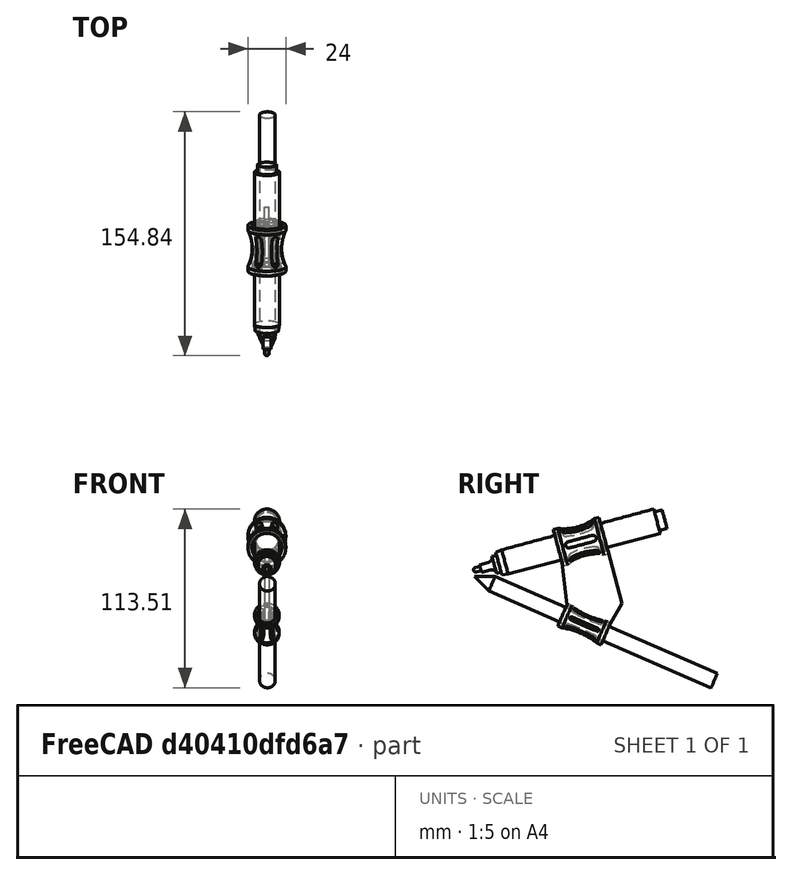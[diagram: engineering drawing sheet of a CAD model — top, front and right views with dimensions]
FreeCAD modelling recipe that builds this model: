
FCSTD DOCUMENT  (FreeCAD 1.0R39109 (Git))
Label: marker_holder_01
License: All rights reserved
LicenseURL: http://www.ohwr.org/attachments/2388/cern_ohl_v_1_2.txt
objects: PartDesign::SubShapeBinder×8, Sketcher::SketchObject×7, PartDesign::Plane×7, PartDesign::Body×5, PartDesign::Revolution×4, PartDesign::Line×3, PartDesign::Pocket×2, PartDesign::PolarPattern×2, PartDesign::Point×2, Mesh::Feature×1, PartDesign::Pad×1
note: 64 computed .brp shape members not serialized (recipe doc carries the construction recipe); baked Part::Feature solids carry a one-line shape summary decoded from their .brp

FEATURE [Mesh::Feature] Pencil_Hand_Pack
  Placement = pos=(0,0,0) rot=(-0.762035,0.457877,-0.457877;1.83927rad)
FEATURE [Sketcher::SketchObject] Sketch
  ArcFitTolerance = 1e-06
  AttachmentSupport = -> [YZ_Plane001]
  FullyConstrained = true
  MakeInternals = false
  MapMode = 5
  Placement = pos=(0,0,0) rot=(0.57735,0.57735,0.57735;2.0944rad)
  sketch-geometry (14):
    g0: LineSegment StartX=125.5 StartY=2e-16 StartZ=0 EndX=125.5 EndY=6 EndZ=0
    g1: LineSegment StartX=125.5 StartY=6 StartZ=0 EndX=120.5 EndY=6 EndZ=0
    g2: LineSegment StartX=120.5 StartY=6 StartZ=0 EndX=120.5 EndY=8 EndZ=0
    g3: LineSegment StartX=120.5 StartY=8 StartZ=0 EndX=28.5 EndY=8 EndZ=0
    g4: LineSegment StartX=28.5 StartY=8 StartZ=0 EndX=20.5 EndY=8 EndZ=0
    g5: LineSegment StartX=20.5 StartY=8 StartZ=0 EndX=16.5 EndY=7.5 EndZ=0
    g6: LineSegment StartX=16.5 StartY=7.5 StartZ=0 EndX=16.5 EndY=5.5 EndZ=0
    g7: LineSegment StartX=16.5 StartY=5.5 StartZ=0 EndX=13.5 EndY=5.5 EndZ=0
    g8: ArcOfCircle CenterX=10.5 CenterY=5.5 CenterZ=0 NormalX=0 NormalY=0 NormalZ=1 AngleXU=0 Radius=3 StartAngle=4.71239 EndAngle=6.28319
    g9: LineSegment StartX=10.5 StartY=2.5 StartZ=0 EndX=4.5 EndY=2.5 EndZ=0
    g10: LineSegment StartX=4.5 StartY=2.5 StartZ=0 EndX=4.5 EndY=1.5 EndZ=0
    g11: LineSegment StartX=4.5 StartY=1.5 StartZ=0 EndX=1.5 EndY=1.5 EndZ=0
    g12: ArcOfCircle CenterX=1.5 CenterY=0 CenterZ=0 NormalX=0 NormalY=0 NormalZ=1 AngleXU=0 Radius=1.5 StartAngle=1.5708 EndAngle=3.14159
    g13: LineSegment StartX=0 StartY=2e-16 StartZ=0 EndX=125.5 EndY=2e-16 EndZ=0
  constraints (40):
    c: Vertical(g0)
    c: Coincident(g0,g1)
    c: Horizontal(g1)
    c: Coincident(g1,g2)
    c: Vertical(g2)
    c: Coincident(g2,g3)
    c: Horizontal(g3)
    c: Coincident(g3,g4)
    c: Horizontal(g4)
    c: Coincident(g4,g5)
    c: Coincident(g5,g6)
    c: Vertical(g6)
    c: Coincident(g6,g7)
    c: Horizontal(g7)
    c: Perpendicular(g7,g8) = 4.71239
    c: Horizontal(g9)
    c: Coincident(g9,g10)
    c: Coincident(g10,g11)
    c: Horizontal(g11)
    c: Tangent(g11,g12) = -1.5708
    c: Perpendicular(g12,g-1)
    c: Radius(g12) = 1.5
    c: DistanceX(g11,g11) = 3
    c: Vertical(g10)
    c: Distance(g10,g10) = 1
    c: DistanceX(g9,g9) = 6
    c: Tangent(g8,g9) = 1.5708
    c: Radius(g8) = 3
    c: DistanceX(g7,g7) = 3
    c: DistanceX(g5,g4) = 4
    c: DistanceX(g4,g4) = 8
    c: DistanceX(g3,g3) = 92
    c: DistanceX(g1,g1) = 5
    c: DistanceY(g0,g0) = 6
    c: Distance(g2,g-1) = 8
    c: Coincident(g12,g-1)
    c: DistanceY(g5,g4) = 0.5
    c: Coincident(g13,g12)
    c: Coincident(g13,g0)
    c: Horizontal(g13)
FEATURE [PartDesign::Revolution] Revolution
  Angle = 360
  Angle2 = 60
  Axis = (0,1,0)
  Base = (0,0,0)
  Placement = pos=(0,0,0) rot=(1,1,1;2.0944rad)
  Profile = -> Sketch
  ReferenceAxis = -> Sketch [H_Axis]
  Refine = true
  Suppressed = false
  Type = 0
FEATURE [PartDesign::Body] Body001  label="Marker"
  AllowCompound = false
  Group = -> [Sketch,Revolution]
  Origin = -> Origin001
  Placement = pos=(74.7,-42.8,49.3) rot=(1,0,0;0.261799rad)
  Tip = -> Revolution
FEATURE [PartDesign::SubShapeBinder] Binder
  BindCopyOnChange = 0
  BindMode = 0
  ClaimChildren = false
  Context = -> Body [Binder.]
  Fuse = false
  MakeFace = true
  OffsetFill = false
  OffsetIntersection = false
  OffsetJoinType = 0
  OffsetOpenResult = false
  PartialLoad = false
  Refine = true
  Relative = true
  Support = -> [Body001]
  _Version = 2
FEATURE [PartDesign::Line] DatumLine
  AttacherType = Attacher::AttachEngineLine
  AttachmentSupport = -> [Binder]
  Length = 20
  MapMode = 19
  Placement = pos=(74.7,78.4237,81.7818) rot=(-0.519988,-0.519988,-0.677661;1.95044rad)
  ResizeMode = 0
FEATURE [PartDesign::Plane] DatumPlane
  AttachmentOffset = pos=(0,0,0) rot=(1,0,0;1.5708rad)
  AttachmentSupport = -> [DatumLine]
  Length = 131.506
  MapMode = 7
  Placement = pos=(74.7,78.4237,81.7818) rot=(1,0,0;3.40339rad)
  ResizeMode = 0
  Width = 193.795
FEATURE [PartDesign::Plane] DatumPlane001
  AttachmentSupport = -> [DatumLine]
  Length = 139.497
  MapMode = 3
  Placement = pos=(74.7,78.4237,81.7818) rot=(0.129428,-0.983106,-0.129428;1.58783rad)
  ResizeMode = 0
  Width = 194.678
FEATURE [PartDesign::Line] DatumLine001
  AttacherType = Attacher::AttachEngineLine
  AttachmentOffset = pos=(0,-104,0) rot=(1,0,0;0.671952rad)
  AttachmentSupport = -> [DatumLine]
  Length = 20
  MapMode = 29
  Placement = pos=(74.7,105.341,-18.6745) rot=(0,0.836286,0.548293;3.14159rad)
  ResizeMode = 0
FEATURE [Sketcher::SketchObject] Sketch001
  ArcFitTolerance = 1e-06
  AttachmentOffset = pos=(0,0,75) rot=(0,0,1;0rad)
  AttachmentSupport = -> [YZ_Plane]
  ExternalGeometry = -> [DatumLine,DatumLine001]
  FullyConstrained = true
  MakeInternals = false
  MapMode = 5
  Placement = pos=(75,0,0) rot=(0.57735,0.57735,0.57735;2.0944rad)
  sketch-geometry (4):
    g0: LineSegment StartX=108.006 StartY=-25.2856 StartZ=0 EndX=-33.221 EndY=36.1217 EndZ=0
    g1: LineSegment StartX=-33.221 StartY=36.1217 StartZ=0 EndX=-42.232 EndY=45.492 EndZ=0
    g2: LineSegment StartX=-42.232 StartY=45.492 StartZ=0 EndX=110 EndY=-20.7003 EndZ=0
    g3: LineSegment StartX=108.006 StartY=-25.2856 StartZ=0 EndX=110 EndY=-20.7003 EndZ=0
  constraints (12):
    c: Coincident(g0,g1)
    c: Coincident(g1,g2)
    c: PointOnObject(g1,g-4)
    c: Distance(g2,g0) = 5
    c: Coincident(g3,g0)
    c: Coincident(g3,g2)
    c: PointOnObject(g2,g-4)
    c: Perpendicular(g2,g3)
    c: Perpendicular(g0,g3)
    c: DistanceX(g2) = 110
    c: Distance(g2,g2) = 166
    c: Distance(g0,g0) = 154
FEATURE [PartDesign::Revolution] Revolution001
  Angle = 360
  Angle2 = 60
  Axis = (0,0.91706,-0.398749)
  Base = (75,-42.232,45.492)
  Placement = pos=(0,0,0) rot=(1,1,1;2.0944rad)
  Profile = -> Sketch001
  ReferenceAxis = -> Sketch001 [Edge3]
  Refine = true
  Reversed = true
  Suppressed = false
  Type = 0
FEATURE [PartDesign::Body] Body  label="Pencil"
  AllowCompound = false
  Group = -> [Binder,DatumLine,DatumPlane,DatumPlane001,DatumLine001,Sketch001,Revolution001]
  Origin = -> Origin
  Tip = -> Revolution001
FEATURE [PartDesign::SubShapeBinder] Binder001
  BindCopyOnChange = 0
  BindMode = 0
  ClaimChildren = false
  Context = -> Body002 [Binder001.]
  Fuse = false
  MakeFace = true
  OffsetFill = false
  OffsetIntersection = false
  OffsetJoinType = 0
  OffsetOpenResult = false
  PartialLoad = false
  Refine = true
  Relative = true
  Support = -> [Body]
  _Version = 2
FEATURE [PartDesign::SubShapeBinder] Binder002
  BindCopyOnChange = 0
  BindMode = 0
  ClaimChildren = false
  Context = -> Body002 [Binder002.]
  Fuse = false
  MakeFace = true
  OffsetFill = false
  OffsetIntersection = false
  OffsetJoinType = 0
  OffsetOpenResult = false
  PartialLoad = false
  Refine = true
  Relative = true
  Support = -> [Body001]
  _Version = 2
FEATURE [PartDesign::Plane] DatumPlane002
  AttachmentOffset = pos=(0,0,-78) rot=(0,0,1;0rad)
  AttachmentSupport = -> [Binder001]
  Length = 130.818
  MapMode = 5
  Placement = pos=(1.42e-14,28.5489,-12.4134) rot=(0,0.836286,0.548293;3.14159rad)
  ResizeMode = 0
  Width = 149.719
FEATURE [PartDesign::Plane] DatumPlane003
  AttachmentOffset = pos=(0,0,-40) rot=(0,0,1;0rad)
  AttachmentSupport = -> [Binder002]
  Length = 129.082
  MapMode = 5
  Placement = pos=(0,54.9787,14.7315) rot=(0,0.608761,0.793353;3.14159rad)
  ResizeMode = 0
  Width = 129.861
FEATURE [PartDesign::Plane] DatumPlane005
  AttachmentOffset = pos=(0,0,0) rot=(0,1,0;1.5708rad)
  AttachmentSupport = -> [Binder001]
  Length = 198.944
  MapMode = 7
  Placement = pos=(75,108.006,-25.2856) rot=(-0.480769,0.733295,0.480769;4.40704rad)
  ResizeMode = 0
  Width = 155.693
FEATURE [Sketcher::SketchObject] Sketch002
  ArcFitTolerance = 1e-06
  AttachmentSupport = -> [DatumPlane005]
  ExternalGeometry = -> [Binder001]
  FullyConstrained = true
  MakeInternals = false
  MapMode = 5
  Placement = pos=(75,108.006,-25.2856) rot=(0.480769,-0.733295,-0.480769;1.87614rad)
  sketch-geometry (11):
    g0: LineSegment [constr] StartX=166 StartY=5 StartZ=0 EndX=1.137e-13 EndY=5 EndZ=0
    g1: LineSegment StartX=105 StartY=-0.8 StartZ=0 EndX=105 EndY=-2.8 EndZ=0
    g2: LineSegment StartX=105 StartY=-2.8 StartZ=0 EndX=102 EndY=-2.8 EndZ=0
    g3: ArcOfCircle CenterX=90 CenterY=-93.95 CenterZ=0 NormalX=0 NormalY=0 NormalZ=1 AngleXU=0 Radius=94.35 StartAngle=1.41114 EndAngle=1.73046
    g4: LineSegment StartX=75 StartY=-0.8 StartZ=0 EndX=75 EndY=-2.8 EndZ=0
    g5: LineSegment [constr] StartX=75 StartY=-0.8 StartZ=0 EndX=105 EndY=-0.8 EndZ=0
    g6: LineSegment [constr] StartX=90 StartY=-93.95 StartZ=0 EndX=90 EndY=-2.8 EndZ=0
    g7: LineSegment [constr] StartX=90 StartY=-2.8 StartZ=0 EndX=90 EndY=-0.8 EndZ=0
    g8: LineSegment [constr] StartX=90 StartY=-0.8 StartZ=0 EndX=90 EndY=0.4 EndZ=0
    g9: ArcOfCircle CenterX=90 CenterY=-47 CenterZ=0 NormalX=0 NormalY=0 NormalZ=1 AngleXU=0 Radius=45.8 StartAngle=1.30569 EndAngle=1.8359
    g10: LineSegment StartX=78 StartY=-2.8 StartZ=0 EndX=75 EndY=-2.8 EndZ=0
  constraints (32):
    c: Coincident(g0,g-5)
    c: Symmetric(g-6,g-6,g0)
    c: Coincident(g1,g2)
    c: Horizontal(g2)
    c: Coincident(g3,g1)
    c: Coincident(g4,g3)
    c: Coincident(g4,g10)
    c: Vertical(g4)
    c: Vertical(g1)
    c: Equal(g1,g4)
    c: DistanceX(g10,g2) = 30
    c: DistanceY(g4,g4) = 2
    c: Coincident(g5,g3)
    c: Coincident(g5,g1)
    c: Coincident(g6,g3)
    c: Symmetric(g2,g10,g6)
    c: Coincident(g7,g6)
    c: Symmetric(g5,g5,g7)
    c: Coincident(g8,g7)
    c: PointOnObject(g8,g3)
    c: Vertical(g8)
    c: Distance(g3,g-3) = 0.8
    c: Distance(g8,g8) = 1.2
    c: PointOnObject(g9,g6)
    c: PointOnObject(g9,g10)
    c: PointOnObject(g10,g9)
    c: Coincident(g2,g9)
    c: Equal(g10,g2)
    c: Distance(g10,g10) = 3
    c: Horizontal(g10)
    c: Distance(g8,g9) = 1.6
    c: DistanceX(g-1,g3) = 90
FEATURE [PartDesign::SubShapeBinder] Binder003
  BindCopyOnChange = 0
  BindMode = 0
  ClaimChildren = false
  Context = -> Body002 [Binder003.]
  Fuse = false
  MakeFace = true
  OffsetFill = false
  OffsetIntersection = false
  OffsetJoinType = 0
  OffsetOpenResult = false
  PartialLoad = false
  Refine = true
  Relative = true
  Support = -> [Body[DatumLine001.]]
  _Version = 2
FEATURE [PartDesign::Revolution] Revolution002
  Angle = 360
  Angle2 = 60
  Axis = (0,0.91706,-0.398749)
  Base = (74.7,105.341,-18.6745)
  Placement = pos=(75,108.006,-25.2856) rot=(-0.480769,0.733295,0.480769;4.40704rad)
  Profile = -> Sketch002
  ReferenceAxis = -> Binder003 [Edge1]
  Refine = true
  Reversed = true
  Suppressed = false
  Type = 0
FEATURE [Sketcher::SketchObject] Sketch003
  ArcFitTolerance = 1e-06
  AttachmentSupport = -> [DatumPlane005]
  ExternalGeometry = -> [Binder003,Revolution002]
  FullyConstrained = true
  MakeInternals = false
  MapMode = 5
  Placement = pos=(75,108.006,-25.2856) rot=(0.480769,-0.733295,-0.480769;1.87614rad)
  sketch-geometry (6):
    g0: ArcOfCircle CenterX=81 CenterY=5 CenterZ=0 NormalX=0 NormalY=0 NormalZ=1 AngleXU=0 Radius=1 StartAngle=1.5708 EndAngle=4.71239
    g1: ArcOfCircle CenterX=99 CenterY=5 CenterZ=0 NormalX=0 NormalY=0 NormalZ=1 AngleXU=0 Radius=1 StartAngle=4.71239 EndAngle=7.85398
    g2: LineSegment StartX=81 StartY=6 StartZ=0 EndX=99 EndY=6 EndZ=0
    g3: LineSegment StartX=81 StartY=4 StartZ=0 EndX=99 EndY=4 EndZ=0
    g4: LineSegment [constr] StartX=78 StartY=5 StartZ=0 EndX=81 EndY=5 EndZ=0
    g5: LineSegment [constr] StartX=102 StartY=5 StartZ=0 EndX=99 EndY=5 EndZ=0
  constraints (14):
    c: Tangent(g0,g2) = 1.5708
    c: Tangent(g0,g3) = -1.5708
    c: Tangent(g1,g2) = 1.5708
    c: Tangent(g1,g3) = -1.5708
    c: Equal(g0,g1)
    c: Horizontal(g2)
    c: Radius(g0) = 1
    c: PointOnObject(g0,g-3)
    c: Symmetric(g-4,g-4,g4)
    c: Coincident(g4,g0)
    c: Symmetric(g-5,g-5,g5)
    c: Coincident(g5,g1)
    c: Equal(g4,g5)
    c: DistanceX(g4,g4) = 3
FEATURE [PartDesign::Pocket] Pocket
  BaseFeature = -> Revolution002
  Direction = (1,1e-16,-1e-16)
  Length = 5
  Length2 = 5
  Placement = pos=(75,108.006,-25.2856) rot=(-0.480769,0.733295,0.480769;4.40704rad)
  Profile = -> Sketch003
  ReferenceAxis = -> Sketch003 [N_Axis]
  Refine = true
  Suppressed = false
  Type = 1
FEATURE [PartDesign::PolarPattern] PolarPattern
  Angle = 360
  Axis = -> Binder003 [Edge1]
  BaseFeature = -> Pocket
  Mode = 0
  Occurrences = 6
  Offset = 120
  Originals = -> [Pocket]
  Placement = pos=(75,108.006,-25.2856) rot=(-0.480769,0.733295,0.480769;4.40704rad)
  Refine = true
  Suppressed = false
  TransformMode = 0
FEATURE [PartDesign::Body] Body002  label="Pencil_holder"
  AllowCompound = false
  Group = -> [Binder001,Binder002,DatumPlane002,DatumPlane003,DatumPlane005,Sketch002,Binder003,Revolution002,Sketch003,Pocket,PolarPattern]
  Origin = -> Origin002
  Tip = -> PolarPattern
FEATURE [PartDesign::SubShapeBinder] Binder004
  BindCopyOnChange = 0
  BindMode = 0
  ClaimChildren = false
  Context = -> Body003 [Binder004.]
  Fuse = false
  MakeFace = true
  OffsetFill = false
  OffsetIntersection = false
  OffsetJoinType = 0
  OffsetOpenResult = false
  PartialLoad = false
  Refine = true
  Relative = true
  Support = -> [Body001]
  _Version = 2
FEATURE [PartDesign::SubShapeBinder] Binder005
  BindCopyOnChange = 0
  BindMode = 0
  ClaimChildren = false
  Context = -> Body003 [Binder005.]
  Fuse = false
  MakeFace = true
  OffsetFill = false
  OffsetIntersection = false
  OffsetJoinType = 0
  OffsetOpenResult = false
  PartialLoad = false
  Refine = true
  Relative = true
  Support = -> [Body002]
  _Version = 2
FEATURE [PartDesign::Plane] DatumPlane006
  AttachmentOffset = pos=(0,0,0) rot=(0,1,0;1.5708rad)
  AttachmentSupport = -> [Binder004]
  Length = 146.981
  MapMode = 8
  Placement = pos=(74.7,71.5235,88.2151) rot=(-0.621515,0.476905,0.621515;4.0316rad)
  ResizeMode = 0
  Width = 146.356
FEATURE [PartDesign::Point] DatumPoint
  AttacherType = Attacher::AttachEnginePoint
  AttachmentSupport = -> [Binder004]
  MapMode = 37
  Placement = pos=(74.7,-42.8,49.3) rot=(0,0,1;0rad)
FEATURE [PartDesign::Point] DatumPoint001
  AttacherType = Attacher::AttachEnginePoint
  AttachmentSupport = -> [Binder004]
  MapMode = 37
  Placement = pos=(74.7,78.4237,81.7818) rot=(0,0,1;0rad)
FEATURE [PartDesign::Line] DatumLine002
  AttacherType = Attacher::AttachEngineLine
  AttachmentSupport = -> [DatumPoint,DatumPoint001]
  Length = 20
  MapMode = 29
  Placement = pos=(74.7,-42.8,49.3) rot=(0,0.608761,0.793353;3.14159rad)
  ResizeMode = 0
FEATURE [Sketcher::SketchObject] Sketch005
  ArcFitTolerance = 1e-06
  AttachmentSupport = -> [DatumPlane006]
  ExternalGeometry = -> [Binder004]
  FullyConstrained = true
  MakeInternals = false
  MapMode = 5
  Placement = pos=(74.7,71.5235,88.2151) rot=(0.621515,-0.476905,-0.621515;2.25159rad)
  sketch-geometry (12):
    g0: LineSegment StartX=35 StartY=4 StartZ=0 EndX=35 EndY=1.5 EndZ=0
    g1: LineSegment StartX=35 StartY=1.5 StartZ=0 EndX=37 EndY=1.5 EndZ=0
    g2: LineSegment StartX=65 StartY=1.5 StartZ=0 EndX=65 EndY=4 EndZ=0
    g3: LineSegment StartX=65 StartY=4 StartZ=0 EndX=62 EndY=4 EndZ=0
    g4: ArcOfCircle CenterX=50 CenterY=31.55 CenterZ=0 NormalX=0 NormalY=0 NormalZ=1 AngleXU=0 Radius=30.05 StartAngle=4.3016 EndAngle=5.12318
    g5: ArcOfCircle CenterX=50 CenterY=32.7 CenterZ=0 NormalX=0 NormalY=0 NormalZ=1 AngleXU=0 Radius=33.8 StartAngle=4.3176 EndAngle=5.10718
    g6: LineSegment StartX=38 StartY=4 StartZ=0 EndX=35 EndY=4 EndZ=0
    g7: LineSegment StartX=63 StartY=1.5 StartZ=0 EndX=65 EndY=1.5 EndZ=0
    g8: LineSegment [constr] StartX=37 StartY=1.5 StartZ=0 EndX=63 EndY=1.5 EndZ=0
    g9: LineSegment [constr] StartX=50 StartY=-1.1 StartZ=0 EndX=50 EndY=1.5 EndZ=0
    g10: LineSegment [constr] StartX=50 StartY=1.5 StartZ=0 EndX=50 EndY=32.7 EndZ=0
    g11: LineSegment [constr] StartX=50 StartY=32.7 StartZ=0 EndX=50 EndY=31.55 EndZ=0
  constraints (37):
    c: Coincident(g0,g1)
    c: Coincident(g7,g2)
    c: Coincident(g2,g3)
    c: Coincident(g6,g0)
    c: Vertical(g0)
    c: Vertical(g2)
    c: Horizontal(g1)
    c: Horizontal(g3)
    c: PointOnObject(g4,g6)
    c: PointOnObject(g5,g7)
    c: Coincident(g3,g4)
    c: PointOnObject(g6,g4)
    c: Coincident(g1,g5)
    c: PointOnObject(g7,g5)
    c: Equal(g6,g3)
    c: Equal(g1,g7)
    c: Equal(g0,g2)
    c: Horizontal(g7)
    c: Horizontal(g6)
    c: Horizontal(g4,g3)
    c: DistanceY(g2,g2) = 2.5
    c: DistanceX(g3,g3) = 3
    c: Distance(g7,g7) = 2
    c: Coincident(g8,g1)
    c: Coincident(g8,g5)
    c: PointOnObject(g9,g5)
    c: Symmetric(g8,g8,g9)
    c: Vertical(g9)
    c: Coincident(g10,g9)
    c: Coincident(g10,g5)
    c: Coincident(g11,g5)
    c: Coincident(g11,g4)
    c: DistanceY(g9,g9) = 2.6
    c: DistanceX(g0,g2) = 30
    c: DistanceY(g-1,g0) = 1.5
    c: Distance(g5,g-2) = 50
    c: Tangent(g4,g8)
FEATURE [PartDesign::Revolution] Revolution003
  Angle = 360
  Angle2 = 60
  Axis = (0,0.965926,0.258819)
  Base = (74.7,-42.8,49.3)
  Placement = pos=(74.7,71.5235,88.2151) rot=(-0.621515,0.476905,0.621515;4.0316rad)
  Profile = -> Sketch005
  ReferenceAxis = -> DatumLine002
  Refine = true
  Reversed = true
  Suppressed = false
  Type = 0
FEATURE [Sketcher::SketchObject] Sketch006
  ArcFitTolerance = 1e-06
  AttachmentSupport = -> [DatumPlane006]
  ExternalGeometry = -> [Revolution003]
  FullyConstrained = true
  MakeInternals = false
  MapMode = 5
  Placement = pos=(74.7,71.5235,88.2151) rot=(0.621515,-0.476905,-0.621515;2.25159rad)
  sketch-geometry (7):
    g0: ArcOfCircle CenterX=58 CenterY=-8 CenterZ=0 NormalX=0 NormalY=0 NormalZ=1 AngleXU=0 Radius=2 StartAngle=4.71239 EndAngle=7.85398
    g1: ArcOfCircle CenterX=42 CenterY=-8 CenterZ=0 NormalX=0 NormalY=0 NormalZ=1 AngleXU=0 Radius=2 StartAngle=1.5708 EndAngle=4.71239
    g2: LineSegment StartX=58 StartY=-10 StartZ=0 EndX=42 EndY=-10 EndZ=0
    g3: LineSegment StartX=58 StartY=-6 StartZ=0 EndX=42 EndY=-6 EndZ=0
    g4: LineSegment [constr] StartX=37 StartY=-8 StartZ=0 EndX=42 EndY=-8 EndZ=0
    g5: LineSegment [constr] StartX=42 StartY=-8 StartZ=0 EndX=58 EndY=-8 EndZ=0
    g6: LineSegment [constr] StartX=58 StartY=-8 StartZ=0 EndX=63 EndY=-8 EndZ=0
  constraints (16):
    c: Tangent(g0,g2) = 1.5708
    c: Tangent(g0,g3) = -1.5708
    c: Tangent(g1,g2) = 1.5708
    c: Tangent(g1,g3) = -1.5708
    c: Equal(g0,g1)
    c: Horizontal(g3)
    c: Radius(g0) = 2
    c: Symmetric(g-4,g-4,g4)
    c: Coincident(g4,g1)
    c: Coincident(g5,g1)
    c: Coincident(g5,g0)
    c: Coincident(g6,g0)
    c: Symmetric(g-3,g-3,g6)
    c: Horizontal(g6)
    c: Equal(g4,g6)
    c: DistanceX(g5,g5) = 16
FEATURE [PartDesign::Pocket] Pocket001
  BaseFeature = -> Revolution003
  Direction = (1,1e-16,-1e-16)
  Length = 5
  Length2 = 5
  Placement = pos=(74.7,71.5235,88.2151) rot=(-0.621515,0.476905,0.621515;4.0316rad)
  Profile = -> Sketch006
  ReferenceAxis = -> Sketch006 [N_Axis]
  Refine = true
  Suppressed = false
  Type = 1
FEATURE [PartDesign::PolarPattern] PolarPattern001
  Angle = 360
  Axis = -> DatumLine002
  BaseFeature = -> Pocket001
  Mode = 0
  Occurrences = 6
  Offset = 120
  Originals = -> [Pocket001]
  Placement = pos=(74.7,71.5235,88.2151) rot=(-0.621515,0.476905,0.621515;4.0316rad)
  Refine = true
  Suppressed = false
  TransformMode = 0
FEATURE [PartDesign::Body] Body003  label="Marker_holder"
  AllowCompound = false
  Group = -> [Binder004,Binder005,DatumPlane006,DatumPoint,DatumPoint001,DatumLine002,Sketch005,Revolution003,Sketch006,Pocket001,PolarPattern001]
  Origin = -> Origin003
  Tip = -> PolarPattern001
FEATURE [PartDesign::SubShapeBinder] Binder006
  BindCopyOnChange = 0
  BindMode = 0
  ClaimChildren = false
  Context = -> Body004 [Binder006.]
  Fuse = false
  MakeFace = true
  OffsetFill = false
  OffsetIntersection = false
  OffsetJoinType = 0
  OffsetOpenResult = false
  PartialLoad = false
  Refine = true
  Relative = true
  Support = -> [Body002]
  _Version = 2
FEATURE [PartDesign::SubShapeBinder] Binder007
  BindCopyOnChange = 0
  BindMode = 0
  ClaimChildren = false
  Context = -> Body004 [Binder007.]
  Fuse = false
  MakeFace = true
  OffsetFill = false
  OffsetIntersection = false
  OffsetJoinType = 0
  OffsetOpenResult = false
  PartialLoad = false
  Refine = true
  Relative = true
  Support = -> [Body003]
  _Version = 2
FEATURE [PartDesign::Plane] DatumPlane007
  AttachmentOffset = pos=(0,0,0) rot=(0,1,0;1.5708rad)
  AttachmentSupport = -> [Binder007]
  Length = 120.322
  MapMode = 7
  Placement = pos=(74.7,33.7831,82.2437) rot=(0.621515,0.476905,0.621515;2.25159rad)
  ResizeMode = 0
  Width = 129.651
FEATURE [Sketcher::SketchObject] Sketch007
  ArcFitTolerance = 1e-06
  AttachmentSupport = -> [DatumPlane007]
  ExternalGeometry = -> [Binder006]
  FullyConstrained = true
  MakeInternals = false
  MapMode = 5
  Placement = pos=(74.7,33.7831,82.2437) rot=(0.621515,0.476905,0.621515;2.25159rad)
  sketch-geometry (11):
    g0: LineSegment StartX=3 StartY=-21.75 StartZ=0 EndX=3 EndY=-56.6648 EndZ=0
    g1: LineSegment StartX=-7.48226 StartY=-67.1471 StartZ=0 EndX=-9.83008 EndY=-65.2795 EndZ=0
    g2: LineSegment StartX=-24 StartY=-21.75 StartZ=0 EndX=-27 EndY=-21.75 EndZ=0
    g3: LineSegment StartX=-27 StartY=-21.75 StartZ=0 EndX=-30.9605 EndY=-48.4716 EndZ=0
    g4: LineSegment StartX=-30.9605 StartY=-48.4716 StartZ=0 EndX=-28.6127 EndY=-50.3392 EndZ=0
    g5: ArcOfCircle CenterX=-12 CenterY=-49.3 CenterZ=0 NormalX=0 NormalY=0 NormalZ=1 AngleXU=0 Radius=30.05 StartAngle=1.16001 EndAngle=1.98159
    g6: LineSegment StartX=-2.84e-14 StartY=-21.75 StartZ=0 EndX=3 EndY=-21.75 EndZ=0
    g7: ArcOfCircle CenterX=8.29377 CenterY=-23.2181 CenterZ=0 NormalX=0 NormalY=0 NormalZ=1 AngleXU=0 Radius=45.8 StartAngle=3.77533 EndAngle=4.30554
    g8: LineSegment [constr] StartX=-28.6127 StartY=-50.3392 StartZ=0 EndX=-9.83008 EndY=-65.2795 EndZ=0
    g9: LineSegment [constr] StartX=-20.2174 StartY=-59.0615 StartZ=0 EndX=-19.2214 EndY=-57.8093 EndZ=0
    g10: LineSegment StartX=-7.48226 StartY=-67.1471 StartZ=0 EndX=3 EndY=-56.6648 EndZ=0
  constraints (30):
    c: Vertical(g0)
    c: Equal(g5,g-7)
    c: PointOnObject(g9,g7)
    c: Symmetric(g8,g8,g9)
    c: Perpendicular(g9,g8)
    c: Distance(g9,g9) = 1.6
    c: Angle(g0,g10) = 2.35619
    c: Coincident(g0,g10)
    c: PointOnObject(g4,g-10)
    c: Symmetric(g-16,g-5,g4)
    c: Coincident(g3,g4)
    c: Symmetric(g-6,g-15,g1)
    c: Perpendicular(g-6,g1)
    c: PointOnObject(g1,g-11)
    c: Coincident(g10,g1)
    c: Coincident(g7,g1)
    c: Coincident(g7,g4)
    c: Perpendicular(g4,g-5)
    c: Coincident(g8,g4)
    c: Coincident(g8,g1)
    c: Symmetric(g-3,g-12,g2)
    c: PointOnObject(g2,g-8)
    c: Perpendicular(g2,g-3)
    c: Coincident(g3,g2)
    c: Coincident(g5,g2)
    c: Symmetric(g-14,g-4,g6)
    c: PointOnObject(g6,g-9)
    c: Perpendicular(g6,g-4)
    c: Coincident(g0,g6)
    c: Coincident(g5,g6)
FEATURE [PartDesign::Pad] Pad
  Direction = (1,-1e-16,1e-16)
  Length = 3
  Length2 = 10
  Midplane = true
  Placement = pos=(74.7,33.7831,82.2437) rot=(0.621515,0.476905,0.621515;2.25159rad)
  Profile = -> Sketch007
  ReferenceAxis = -> Sketch007 [N_Axis]
  Refine = true
  Suppressed = false
  Type = 0
FEATURE [PartDesign::Body] Body004  label="Bridge"
  AllowCompound = false
  Group = -> [Binder006,Binder007,DatumPlane007,Sketch007,Pad]
  Origin = -> Origin004
  Tip = -> Pad
